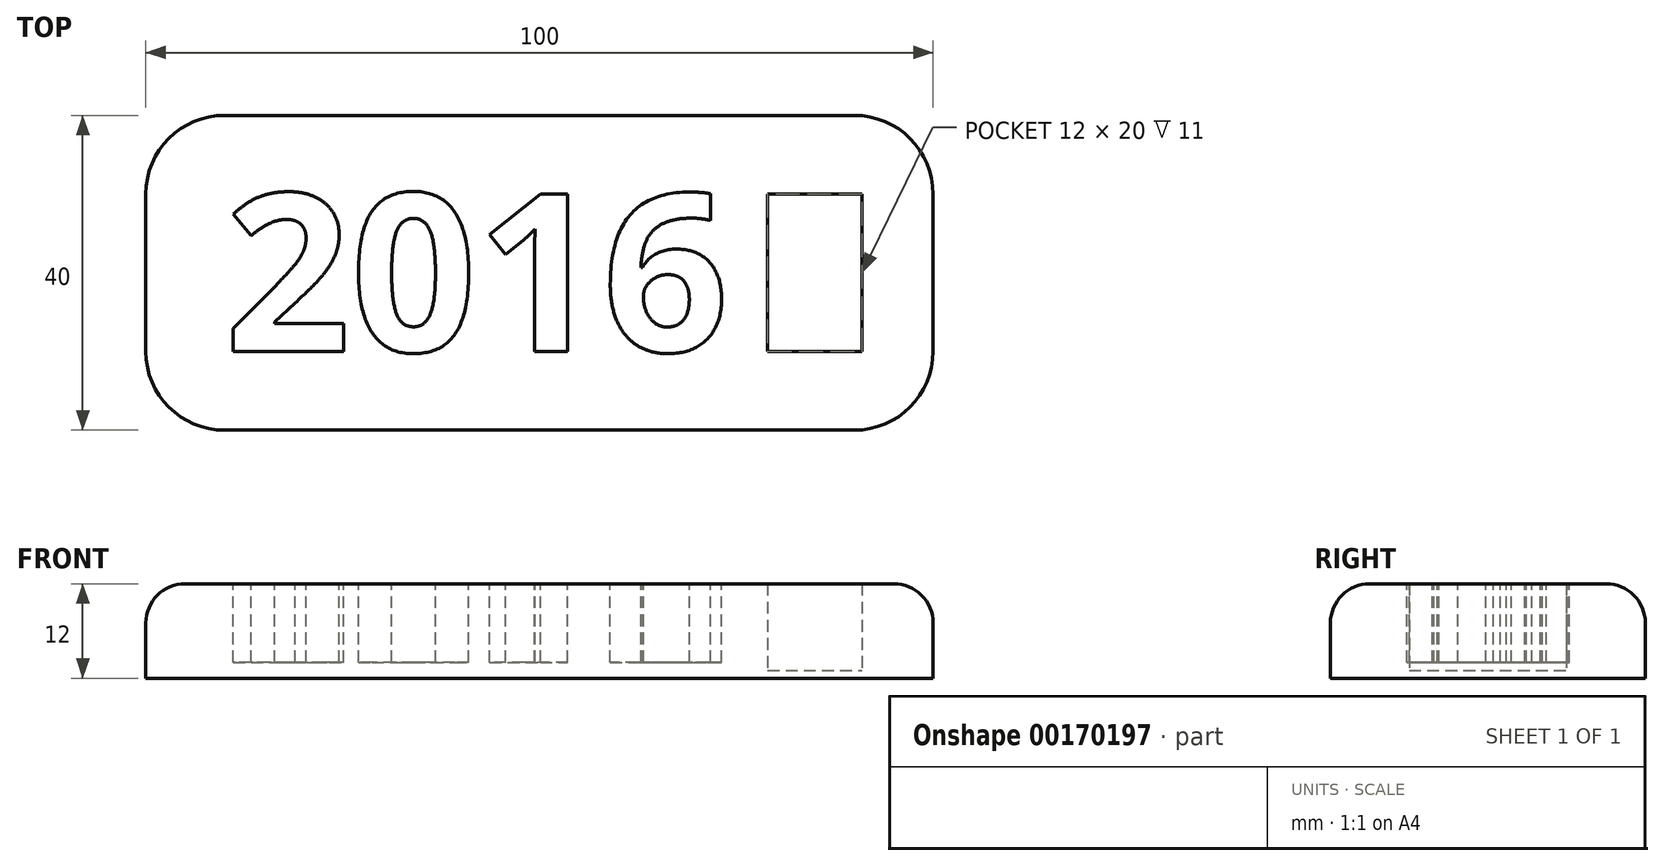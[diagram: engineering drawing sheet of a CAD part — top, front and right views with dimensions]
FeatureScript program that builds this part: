
annotation { "Feature Type Name" : "Feature", "Feature Type Description" : "" }
export const myFeature = defineFeature(function(context is Context, id is Id, definition is map)
    precondition{}
    {
        {
            var Q0;
            Q0=qCreatedBy(makeId("Top.planeOp"),FACE);
            var sketch = newSketch(context, id + "F0", { "sketchPlane" : qUnion([Q0])});
            skLineSegment(sketch, "E0.bottom", {"start": v(50, -20) * mm, "end": v(-50, -20) * mm});
            skLineSegment(sketch, "E0.top", {"start": v(50, 20) * mm, "end": v(-50, 20) * mm});
            skLineSegment(sketch, "E0.left", {"start": v(50, -20) * mm, "end": v(50, 20) * mm});
            skLineSegment(sketch, "E0.right", {"start": v(-50, -20) * mm, "end": v(-50, 20) * mm});
            skPoint(sketch, "E0.middle", {"position": v(0, 0) * mm});
            skLineSegment(sketch, "E1", {"start": v(50, 0) * mm, "end": v(35, 0) * mm});
            skPoint(sketch, "E1.endSnap0", {"position": v(50, 0) * mm});
            skLineSegment(sketch, "E2.bottom", {"start": v(29, -10) * mm, "end": v(41, -10) * mm});
            skLineSegment(sketch, "E2.top", {"start": v(29, 10) * mm, "end": v(41, 10) * mm});
            skLineSegment(sketch, "E2.left", {"start": v(29, -10) * mm, "end": v(29, 10) * mm});
            skLineSegment(sketch, "E2.right", {"start": v(41, -10) * mm, "end": v(41, 10) * mm});
            skPoint(sketch, "E2.middle", {"position": v(35, 0) * mm});
            skSolve(sketch);
        }
        {
            var Q0;
            {var subQ3=sQuery(id+"F0.wireOp",EDGE,"E0.bottom");Q0=makeQuery(id+"F0.imprint","IMPRINT",FACE,{"disambiguationData":[TD([[makeQuery(id+"F0.imprint","IMPRINT",EDGE,{"derivedFrom":subQ3}),-1.0]])]});}
            extrude(context, id + "F1", {"entities" : qUnion([Q0]), "depth" : 12 * mm});
        }
        {
            var Q0;
            {var subQ1=sQuery(id+"F0.wireOp",EDGE,"E2.bottom");Q0=makeQuery(id+"F0.imprint","IMPRINT",FACE,{"disambiguationData":[TD([[makeQuery(id+"F0.imprint","IMPRINT",EDGE,{"derivedFrom":subQ1}),1.0]])]});}
            extrude(context, id + "F2", {"entities" : qUnion([Q0]), "operationType" : NewBodyOperationType.ADD, "depth" : 1 * mm});
        }
        {
            var Q0;
            Q0=makeQuery(id+"F1.opExtrude","SWEPT_EDGE",EDGE,{"disambiguationData":[OSD([sQuery(id+"F0.wireOp",EDGE,"E0.bottom"),sQuery(id+"F0.wireOp",EDGE,"E0.left")])]});
            var Q1;
            Q1=makeQuery(id+"F1.opExtrude","SWEPT_EDGE",EDGE,{"disambiguationData":[OSD([sQuery(id+"F0.wireOp",EDGE,"E0.top"),sQuery(id+"F0.wireOp",EDGE,"E0.left")])]});
            var Q2;
            Q2=makeQuery(id+"F1.opExtrude","SWEPT_EDGE",EDGE,{"disambiguationData":[OSD([sQuery(id+"F0.wireOp",EDGE,"E0.top"),sQuery(id+"F0.wireOp",EDGE,"E0.right")])]});
            var Q3;
            Q3=makeQuery(id+"F1.opExtrude","SWEPT_EDGE",EDGE,{"disambiguationData":[OSD([sQuery(id+"F0.wireOp",EDGE,"E0.bottom"),sQuery(id+"F0.wireOp",EDGE,"E0.right")])]});
            fillet(context, id + "F3", {"entities" : qUnion([Q0, Q1, Q2, Q3]), "radius" : 10 * mm, "tangentPropagation" : true, "allowEdgeOverflow" : false});
        }
        {
            var Q0;
            Q0=makeQuery(id+"F1.opExtrude","CAP_EDGE",EDGE,{"disambiguationData":[OSD([sQuery(id+"F0.wireOp",EDGE,"E0.top")])],"isStart":false});
            fillet(context, id + "F4", {"entities" : qUnion([Q0]), "radius" : 5 * mm, "tangentPropagation" : true, "allowEdgeOverflow" : false});
        }
        {
            var Q0;
            Q0=makeQuery(id+"F1.opExtrude","CAP_FACE",FACE,{"disambiguationData":[OSD([sQuery(id+"F0.wireOp",EDGE,"E0.bottom"),sQuery(id+"F0.wireOp",EDGE,"E0.top"),sQuery(id+"F0.wireOp",EDGE,"E0.left"),sQuery(id+"F0.wireOp",EDGE,"E0.right"),sQuery(id+"F0.wireOp",EDGE,"E2.bottom"),sQuery(id+"F0.wireOp",EDGE,"E2.top"),sQuery(id+"F0.wireOp",EDGE,"E2.left"),sQuery(id+"F0.wireOp",EDGE,"E2.right")])],"isStart":false});
            var sketch = newSketch(context, id + "F5", { "sketchPlane" : qUnion([Q0])});
            skText(sketch, "E3", { "text": "2016", "fontName": "OpenSans-Bold.ttf"});
            const initialGuessF5  = {"E3": [-0.04, -0.01, 1, 0, 0.02019]};
            skSetInitialGuess(sketch, initialGuessF5);
            skSolve(sketch);
        }
        {
            var Q0;
            Q0 = qSketchRegion(id + "F5", true);
            extrude(context, id + "F6", {"entities" : qUnion([Q0]), "operationType" : NewBodyOperationType.REMOVE, "oppositeDirection" : true, "depth" : 10 * mm});
        }
    });
